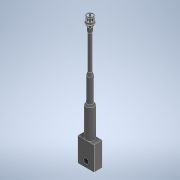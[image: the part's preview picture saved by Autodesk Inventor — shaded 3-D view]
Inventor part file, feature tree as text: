
AUTODESK INVENTOR PART (.ipt)
format: ipt  version: 2022 (Build 260153000, 153)  size: 727,552 bytes
history: native  units: mm
features: sketch x18, extrude x17, chamfer x5, fillet x4
ambient origin geometry x8: Origin, YZ Plane, XZ Plane, XY Plane, X Axis, Y Axis, Z Axis, Center Point
bodies: Solid1 (feature_tree)
feature tree (44):
  extrude  "Extrusion1"  Depth=45.0mm TaperAngle=0.0deg
  extrude  "Extrusion2"  Depth=40.0mm TaperAngle=0.0deg
  extrude  "Extrusion3"  Depth=50.0mm TaperAngle=0.0deg
  extrude  "Extrusion4"  Depth=1.5mm TaperAngle=0.0deg
  chamfer  "Chamfer1"  Distance=2.1mm Angle=45.0deg
  chamfer  "Chamfer2"  Distance=1.5mm Angle=45.0deg
  extrude  "Extrusion5"  Depth=7.0mm TaperAngle=0.0deg
  chamfer  "Chamfer3"  Distance=5.0mm Angle=45.0deg
  chamfer  "Chamfer4"  Distance=0.5mm Angle=45.0deg
  extrude  "Extrusion6"  Depth=0.2mm
  extrude  "Extrusion7"  Depth=2.0mm
  extrude  "Extrusion8"  Depth=1.0mm
  extrude  "Extrusion9"  Depth=1.5mm
  extrude  "Extrusion10"  TaperAngle=0.0deg  [1 undecoded]
  extrude  "Extrusion11"  Depth=1.0mm
  chamfer  "Chamfer5"  Distance=1.5mm
  fillet  "Fillet1"  Radius=0.5mm
  fillet  "Fillet2"  Radius=0.5mm
  fillet  "Fillet3"  Radius=0.5mm
  extrude  "Extrusion12"  Depth=10.0mm
  extrude  "Extrusion13"  Depth=10.0mm
  extrude  "Extrusion14"  TaperAngle=0.0deg  [1 undecoded]
  extrude  "Extrusion15"  Depth=10.0mm TaperAngle=0.0deg
  fillet  "Fillet5"  Radius=10.0mm
  sketch  "Sketch16"  dims[d51=0.5mm]
  extrude  "Extrusion16"  Depth=10.0mm TaperAngle=0.0deg
  extrude  "Extrusion17"  Depth=10.0mm TaperAngle=45.0deg
  sketch  "Sketch1"  dims[d0=12.2mm d1=45.0mm d2=0.0mm]
  sketch  "Sketch2"  dims[d3=8.0mm d4=40.0mm d5=0.0mm]
  sketch  "Sketch3"  dims[d6=5.0mm d7=50.0mm d8=0.0mm]
  sketch  "Sketch4"  dims[d9=12.0mm d10=12.0mm d11=0.0mm d12=2.1mm d13=2.5mm d14=45.0deg d15=1.5mm d16=5.0mm d17=45.0deg]
  sketch  "Sketch5"  dims[d18=6.0mm d19=7.0mm d20=0.0mm d21=5.0mm d22=3.0mm d23=45.0deg d24=0.5mm d25=0.5mm d26=45.0deg]
  sketch  "Sketch6"  dims[d29=0.0mm d30=0.0mm d31=0.2mm]
  sketch  "Sketch7"  dims[d32=100.0mm d34=360.0deg d36=2.0mm]
  sketch  "Sketch8"  dims[d37=5.0mm d38=0.0mm d39=1.0mm]
  sketch  "Sketch9"  dims[d40=2.0mm d41=1.5mm]
  sketch  "Sketch10"  dims[d42=1.5mm d43=0.0mm d44=0.0mm]
  sketch  "Sketch11"  dims[d45=1.0mm d46=1.0mm]
  sketch  "Sketch12"  dims[d47=0.5mm]
  sketch  "Sketch13"  dims[d48=2.0mm]
  sketch  "Sketch14"  dims[d49=0.5mm]
  sketch  "Sketch15"  dims[d50=0.5mm]
  sketch  "Sketch17"  dims[d52=1.0mm]
  sketch  "Sketch18"  dims[d53=2.0mm d54=1.5mm d55=0.5mm d56=0.5mm d57=0.5mm d58=5.0mm d59=1.0mm d60=5.0mm d61=0.0mm d62=0.0mm d63=10.0mm d64=0.0mm d65=10.0mm d66=7.0mm d67=0.0mm d68=2.5mm d69=1.0mm d70=45.0deg d71=0.05mm d72=2.0mm d73=1.0mm d74=100.0mm d76=360.0deg d78=0.0mm d79=0.0mm d80=0.5mm d81=0.1mm d82=0.5mm d83=0.5mm d84=0.0mm d85=0.0mm d86=2.0mm d87=0.5mm d88=0.5mm d89=4.9mm d90=0.5mm d91=0.0mm d92=0.0mm d94=0.25mm d95=11.0mm d96=0.0mm d98=0.5mm d99=2.0mm d100=6.1mm d101=12.0mm d102=12.2mm d103=24.0mm d104=35.0mm d105=0.0mm d106=100.0mm d108=360.0deg d110=3.0mm d111=5.0mm d112=8.0mm d113=35.0mm d114=0.0mm]
note: 2 required parameter values undecoded (feature->parameter linkage not recoverable at this tier; creation-order binding heuristic only, values carry confidence <= 0.55)
